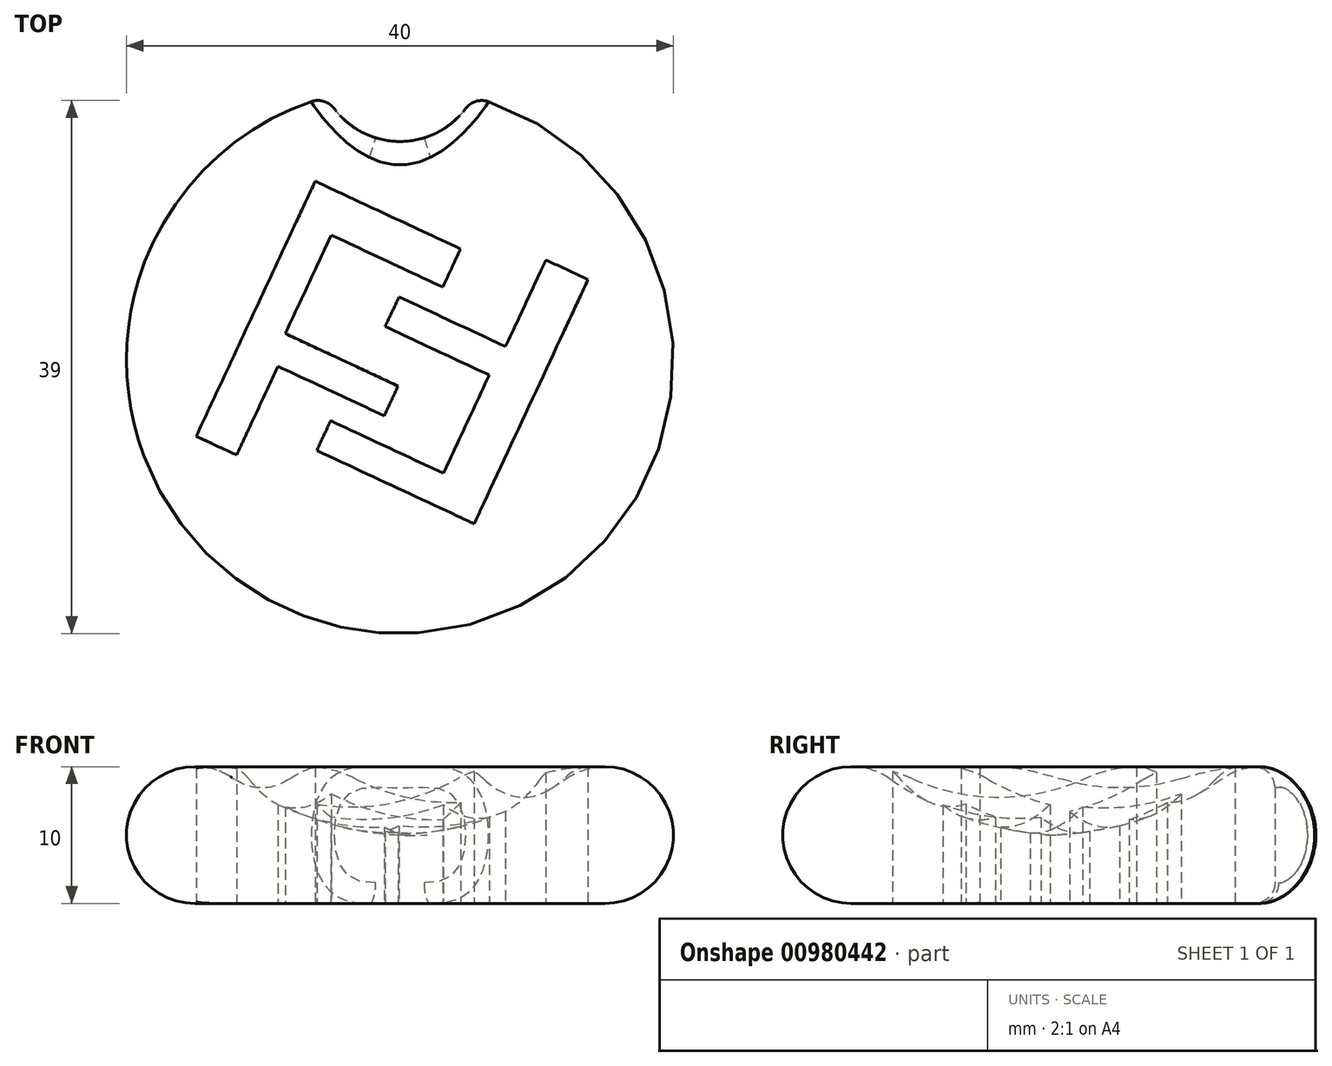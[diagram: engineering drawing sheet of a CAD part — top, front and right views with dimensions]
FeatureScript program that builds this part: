
annotation { "Feature Type Name" : "Feature", "Feature Type Description" : "" }
export const myFeature = defineFeature(function(context is Context, id is Id, definition is map)
    precondition{}
    {
        {
            var Q0;
            Q0=qCreatedBy(makeId("Front.planeOp"),FACE);
            var sketch = newSketch(context, id + "F0", { "sketchPlane" : qUnion([Q0])});
            skArc(sketch, "E0", {"start": v(-12.14, 9.1) * mm, "mid": v(-19.77, 6.5) * mm, "end": v(-15, 0) * mm});
            skArc(sketch, "E1", {"start": v(-12.14, 9.1) * mm, "mid": v(-6.36, 6.19) * mm, "end": v(0, 5) * mm});
            skLineSegment(sketch, "E2", {"start": v(0, 0) * mm, "end": v(0, 5) * mm});
            skLineSegment(sketch, "E3", {"start": v(0, 5) * mm, "end": v(0, 0) * mm});
            skLineSegment(sketch, "E4", {"start": v(-15, 0) * mm, "end": v(0, 0) * mm});
            skSolve(sketch);
        }
        {
            var Q0;
            Q0 = qSketchRegion(id + "F0", true);
            var Q1;
            Q1=sQuery(id+"F0.wireOp",EDGE,"E3");
            revolve(context, id + "F1", {"surfaceOperationType" : NewSurfaceOperationType.NEW, "entities" : qUnion([Q0]), "axis" : qUnion([Q1]), "revolveType" : RevolveType.FULL});
        }
        {
            var Q0;
            Q0=qCreatedBy(makeId("Top.planeOp"),FACE);
            var sketch = newSketch(context, id + "F2", { "sketchPlane" : qUnion([Q0])});
            skLineSegment(sketch, "E5", {"start": v(9.9, 5.65) * mm, "end": v(7.73, 1) * mm});
            skLineSegment(sketch, "E6", {"start": v(7.73, 1) * mm, "end": v(3.83, 2.81) * mm});
            skLineSegment(sketch, "E7", {"start": v(3.83, 2.81) * mm, "end": v(-0.06, 4.63) * mm});
            skLineSegment(sketch, "E8", {"start": v(-0.06, 4.63) * mm, "end": v(-0.57, 3.54) * mm});
            skLineSegment(sketch, "E9", {"start": v(-0.57, 3.54) * mm, "end": v(-1.08, 2.45) * mm});
            skLineSegment(sketch, "E10", {"start": v(-1.08, 2.45) * mm, "end": v(2.82, 0.64) * mm});
            skLineSegment(sketch, "E11", {"start": v(2.82, 0.64) * mm, "end": v(6.53, -1.1) * mm});
            skLineSegment(sketch, "E12", {"start": v(6.53, -1.1) * mm, "end": v(4.86, -4.68) * mm});
            skLineSegment(sketch, "E13", {"start": v(4.86, -4.68) * mm, "end": v(3.18, -8.28) * mm});
            skLineSegment(sketch, "E14", {"start": v(3.18, -8.28) * mm, "end": v(-0.99, -6.34) * mm});
            skLineSegment(sketch, "E15", {"start": v(-0.99, -6.34) * mm, "end": v(-5.06, -4.44) * mm});
            skLineSegment(sketch, "E16", {"start": v(-5.06, -4.44) * mm, "end": v(-5.57, -5.52) * mm});
            skLineSegment(sketch, "E17", {"start": v(-5.57, -5.52) * mm, "end": v(-6.08, -6.6) * mm});
            skLineSegment(sketch, "E18", {"start": v(-6.08, -6.6) * mm, "end": v(-0.37, -9.27) * mm});
            skLineSegment(sketch, "E19", {"start": v(-0.37, -9.27) * mm, "end": v(5.43, -11.98) * mm});
            skLineSegment(sketch, "E20", {"start": v(5.43, -11.98) * mm, "end": v(10.5, -1.1) * mm});
            skLineSegment(sketch, "E21", {"start": v(10.5, -1.1) * mm, "end": v(13.76, 5.9) * mm});
            skLineSegment(sketch, "E22", {"start": v(13.76, 5.9) * mm, "end": v(12.33, 6.56) * mm});
            skLineSegment(sketch, "E23", {"start": v(-14.9, -5.57) * mm, "end": v(-11.95, -6.94) * mm});
            skLineSegment(sketch, "E24", {"start": v(-11.95, -6.94) * mm, "end": v(-11.15, -5.24) * mm});
            skLineSegment(sketch, "E25", {"start": v(-11.15, -5.24) * mm, "end": v(-8.92, -0.45) * mm});
            skLineSegment(sketch, "E26", {"start": v(-8.92, -0.45) * mm, "end": v(-5.03, -2.26) * mm});
            skLineSegment(sketch, "E27", {"start": v(-5.03, -2.26) * mm, "end": v(-1.14, -4.07) * mm});
            skLineSegment(sketch, "E28", {"start": v(-1.14, -4.07) * mm, "end": v(-0.64, -2.99) * mm});
            skLineSegment(sketch, "E29", {"start": v(-0.64, -2.99) * mm, "end": v(-0.13, -1.9) * mm});
            skLineSegment(sketch, "E30", {"start": v(-0.13, -1.9) * mm, "end": v(-4.48, 0.13) * mm});
            skLineSegment(sketch, "E31", {"start": v(-4.48, 0.13) * mm, "end": v(-8.38, 1.95) * mm});
            skLineSegment(sketch, "E32", {"start": v(-8.38, 1.95) * mm, "end": v(-6.7, 5.55) * mm});
            skLineSegment(sketch, "E33", {"start": v(-6.7, 5.55) * mm, "end": v(-5.02, 9.15) * mm});
            skLineSegment(sketch, "E34", {"start": v(-5.02, 9.15) * mm, "end": v(-0.94, 7.24) * mm});
            skLineSegment(sketch, "E35", {"start": v(-0.94, 7.24) * mm, "end": v(3.14, 5.34) * mm});
            skLineSegment(sketch, "E36", {"start": v(3.14, 5.34) * mm, "end": v(3.64, 6.43) * mm});
            skLineSegment(sketch, "E37", {"start": v(3.64, 6.43) * mm, "end": v(4.44, 8.13) * mm});
            skLineSegment(sketch, "E38", {"start": v(-6.2, 13.1) * mm, "end": v(4.44, 8.13) * mm});
            skLineSegment(sketch, "E39", {"start": v(10.68, 7.33) * mm, "end": v(12.33, 6.56) * mm});
            skLineSegment(sketch, "E40", {"start": v(-6.2, 13.1) * mm, "end": v(-14.9, -5.57) * mm});
            skLineSegment(sketch, "E41", {"start": v(10.68, 7.33) * mm, "end": v(9.9, 5.65) * mm});
            skSolve(sketch);
        }
        {
            var Q0;
            Q0 = qSketchRegion(id + "F2", true);
            extrude(context, id + "F3", {"entities" : qUnion([Q0]), "operationType" : NewBodyOperationType.REMOVE, "endBound" : BoundingType.SYMMETRIC, "depth" : 25 * mm, "offsetDistance" : 25 * mm});
        }
        {
            var Q0;
            Q0=qCreatedBy(makeId("Top.planeOp"),FACE);
            var sketch = newSketch(context, id + "F4", { "sketchPlane" : qUnion([Q0])});
            skCircle(sketch, "E42", {"center": v(0, 22) * mm, "radius": 6 * mm});
            skSolve(sketch);
        }
        {
            var Q0;
            Q0 = qSketchRegion(id + "F4", true);
            extrude(context, id + "F5", {"entities" : qUnion([Q0]), "operationType" : NewBodyOperationType.REMOVE, "endBound" : BoundingType.SYMMETRIC, "depth" : 25 * mm, "offsetDistance" : 25 * mm});
        }
        {
            var Q0;
            Q0=makeQuery(id+"F5.boolean.opBoolean","INTERSECT",EDGE,{"derivedFrom":[makeQuery(id+"F1.opRevolve","SWEPT_FACE",FACE,{"disambiguationData":[OSD([sQuery(id+"F0.wireOp",EDGE,"E0")])]}),makeQuery(id+"F5.opExtrude","SWEPT_FACE",FACE,{"disambiguationData":[OSD([sQuery(id+"F4.wireOp",EDGE,"E42")])]})]});
            fillet(context, id + "F6", {"entities" : qUnion([Q0]), "radius" : 1.5 * mm, "tangentPropagation" : true, "allowEdgeOverflow" : false});
        }
    });
